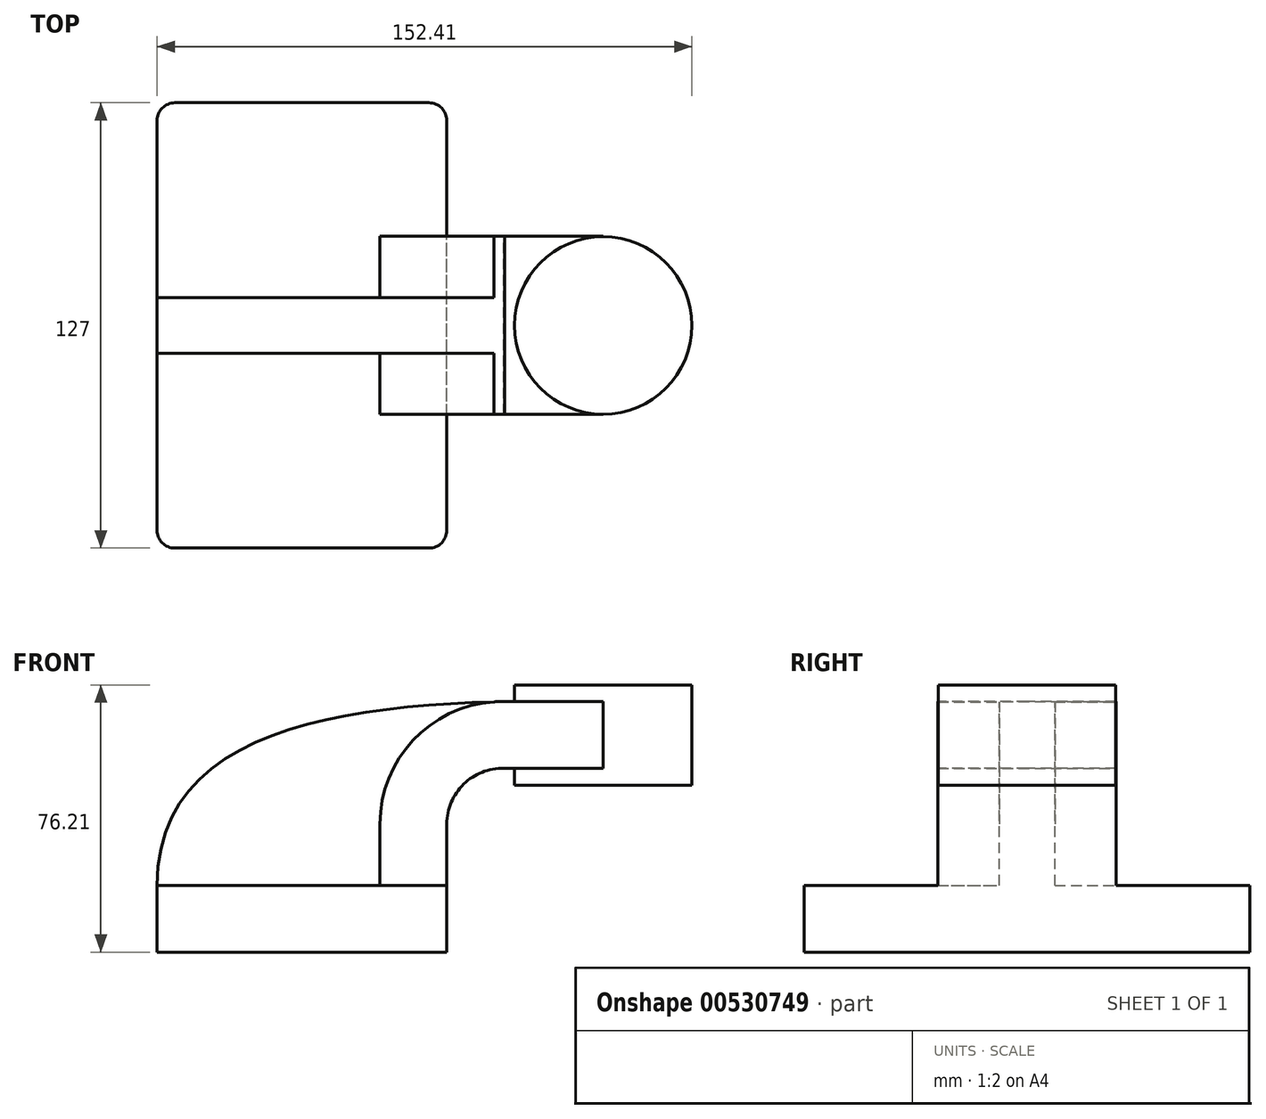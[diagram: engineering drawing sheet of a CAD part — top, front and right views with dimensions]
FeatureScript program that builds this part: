
annotation { "Feature Type Name" : "Feature", "Feature Type Description" : "" }
export const myFeature = defineFeature(function(context is Context, id is Id, definition is map)
    precondition{}
    {
        {
            var Q0;
            Q0=qCreatedBy(makeId("Front.planeOp"),FACE);
            var sketch = newSketch(context, id + "F0", { "sketchPlane" : qUnion([Q0])});
            skLineSegment(sketch, "E0.bottom", {"start": v(-41.28, 9.52) * mm, "end": v(41.27, 9.53) * mm});
            skLineSegment(sketch, "E0.top", {"start": v(-41.28, -9.53) * mm, "end": v(41.28, -9.53) * mm});
            skLineSegment(sketch, "E0.left", {"start": v(-41.28, 9.52) * mm, "end": v(-41.28, -9.53) * mm});
            skLineSegment(sketch, "E0.right", {"start": v(41.27, 9.53) * mm, "end": v(41.28, -9.52) * mm});
            skPoint(sketch, "E0.middle", {"position": v(0, 0) * mm});
            skLineSegment(sketch, "E1.bottom", {"start": v(60.32, 38.1) * mm, "end": v(111.12, 38.1) * mm});
            skLineSegment(sketch, "E1.top", {"start": v(60.32, 66.68) * mm, "end": v(111.12, 66.68) * mm});
            skLineSegment(sketch, "E1.left", {"start": v(60.32, 38.1) * mm, "end": v(60.32, 66.67) * mm});
            skLineSegment(sketch, "E1.right", {"start": v(111.12, 38.1) * mm, "end": v(111.12, 66.68) * mm});
            skPoint(sketch, "E1.middle", {"position": v(85.72, 52.39) * mm});
            skLineSegment(sketch, "E2", {"start": v(41.27, 9.53) * mm, "end": v(41.27, 27) * mm});
            skArc(sketch, "E3", {"start": v(41.27, 27) * mm, "mid": v(46.07, 38.37) * mm, "end": v(57.55, 42.88) * mm});
            skLineSegment(sketch, "E4", {"start": v(57.55, 42.88) * mm, "end": v(85.83, 42.88) * mm});
            skLineSegment(sketch, "E5.0", {"start": v(57.75, 61.93) * mm, "end": v(85.83, 61.93) * mm});
            skArc(sketch, "E5.1", {"start": v(22.22, 27) * mm, "mid": v(32.67, 51.91) * mm, "end": v(57.75, 61.93) * mm});
            skLineSegment(sketch, "E5.2", {"start": v(22.22, 9.53) * mm, "end": v(22.22, 27) * mm});
            skFitSpline(sketch, "E6", {"points": [v(-41.28, 9.52) * mm, v(57.75, 61.93) * mm], "startDerivative": vector(-0.11, 131.08) * mm, "endDerivative": vector(145.21, 3.42) * mm});
            skLineSegment(sketch, "E7", {"start": v(85.83, 38.1) * mm, "end": v(85.83, 66.68) * mm});
            skSolve(sketch);
        }
        {
            var Q0;
            Q0=makeQuery(id+"F0.imprint","IMPRINT",FACE,{"disambiguationData":[TD([[makeQuery(id+"F0.imprint","IMPRINT",EDGE,{"derivedFrom":sQuery(id+"F0.wireOp",EDGE,"E0.top")}),1.0]])]});
            extrude(context, id + "F1", {"entities" : qUnion([Q0]), "endBound" : BoundingType.SYMMETRIC, "depth" : 127 * mm, "offsetDistance" : 25.4 * mm});
        }
        {
            var Q0;
            {var subQ1=sQuery(id+"F0.wireOp",EDGE,"E2");Q0=makeQuery(id+"F0.imprint","IMPRINT",FACE,{"disambiguationData":[TD([[makeQuery(id+"F0.imprint","IMPRINT",EDGE,{"derivedFrom":subQ1}),1.0]])]});}
            var Q1;
            {var subQ0=sQuery(id+"F0.wireOp",EDGE,"E4");var subQ1=sQuery(id+"F0.wireOp",EDGE,"E1.left");var subQ2=makeQuery(id+"F0.imprint","INTERSECT",VERTEX,{"derivedFrom":[subQ1,subQ0]});Q1=makeQuery(id+"F0.imprint","IMPRINT",FACE,{"disambiguationData":[TD([[makeQuery(id+"F0.imprint","IMPRINT",EDGE,{"disambiguationData":[TD([[subQ2,-1.0]])],"derivedFrom":subQ1}),-1.0]])]});}
            extrude(context, id + "F2", {"entities" : qUnion([Q0, Q1]), "operationType" : NewBodyOperationType.ADD, "endBound" : BoundingType.SYMMETRIC, "depth" : 50.8 * mm, "offsetDistance" : 25.4 * mm});
        }
        {
            var Q0;
            {var subQ4=sQuery(id+"F0.wireOp",EDGE,"E1.right");Q0=makeQuery(id+"F0.imprint","IMPRINT",FACE,{"disambiguationData":[TD([[makeQuery(id+"F0.imprint","IMPRINT",EDGE,{"derivedFrom":subQ4}),1.0]])]});}
            var Q1;
            Q1=sQuery(id+"F0.wireOp",EDGE,"E7");
            revolve(context, id + "F3", {"operationType" : NewBodyOperationType.ADD, "entities" : qUnion([Q0]), "axis" : qUnion([Q1]), "revolveType" : RevolveType.FULL});
        }
        {
            var Q0;
            {var subQ3=sQuery(id+"F0.wireOp",EDGE,"E5.2");Q0=makeQuery(id+"F0.imprint","IMPRINT",FACE,{"disambiguationData":[TD([[makeQuery(id+"F0.imprint","IMPRINT",EDGE,{"derivedFrom":subQ3}),1.0]])]});}
            extrude(context, id + "F4", {"entities" : qUnion([Q0]), "operationType" : NewBodyOperationType.ADD, "endBound" : BoundingType.SYMMETRIC, "depth" : 15.88 * mm, "offsetDistance" : 25.4 * mm});
        }
        {
            var Q0;
            Q0=makeQuery(id+"F1.opExtrude","CAP_EDGE",EDGE,{"disambiguationData":[OSD([sQuery(id+"F0.wireOp",EDGE,"E0.left")])],"isStart":false});
            var Q1;
            Q1=makeQuery(id+"F1.opExtrude","CAP_EDGE",EDGE,{"disambiguationData":[OSD([sQuery(id+"F0.wireOp",EDGE,"E0.right")])],"isStart":false});
            var Q2;
            Q2=makeQuery(id+"F1.opExtrude","CAP_EDGE",EDGE,{"disambiguationData":[OSD([sQuery(id+"F0.wireOp",EDGE,"E0.right")])],"isStart":true});
            var Q3;
            Q3=makeQuery(id+"F1.opExtrude","CAP_EDGE",EDGE,{"disambiguationData":[OSD([sQuery(id+"F0.wireOp",EDGE,"E0.left")])],"isStart":true});
            fillet(context, id + "F5", {"entities" : qUnion([Q0, Q1, Q2, Q3]), "radius" : 5.08 * mm, "tangentPropagation" : true, "allowEdgeOverflow" : false});
        }
    });
